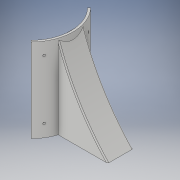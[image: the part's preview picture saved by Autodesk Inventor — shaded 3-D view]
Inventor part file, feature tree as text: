
AUTODESK INVENTOR PART (.ipt)
format: ipt  version: 2017 (Build 210142000, 142)  size: 180,736 bytes
history: native  units: in
note: dims shown in document units (in); Inventor stores cm internally (conversion verified against a paired STEP export)
features: sketch x5, extrude x3, plane x3, hole x2, shell x1, fillet x1
ambient origin geometry x8: Origin, YZ Plane, XZ Plane, XY Plane, X Axis, Y Axis, Z Axis, Center Point
bodies: Solid1 (feature_tree)
feature tree (15):
  extrude  "Extrusion1"  Depth=10.0in
  shell  "Shell2"  Thickness=3.0in
  extrude  "Extrusion6"  Depth=0.1in TaperAngle=0.0deg
  plane  "Work Plane4"
  extrude  "Extrusion7"  Depth=9.5in
  plane  "Work Plane5"
  hole  "Hole3"  [1 undecoded]
  fillet  "Fillet2"  Radius=0.25in
  plane  "Work Plane7"
  hole  "Hole5"  [1 undecoded]
  sketch  "Sketch1"  dims[d0=6.0in d1=10.0in d2=3.0in d3=0.0in]
  sketch  "Sketch10"  dims[d6=0.1in d53=0.1in d54=0.0in]
  sketch  "Sketch11"  dims[d55=10.0in d56=9.5in]
  sketch  "Sketch12"  dims[d57=9.9in d58=0.0in d59=0.25in d60=0.25in]
  sketch  "Sketch14"  dims[d61=0.25in d62=0.75in d63=0.375in d64=0.25in d65=0.5635in d66=1.0in d67=0.8108in d77=0.125in d78=0.25in d79=0.25in d80=0.25in d81=0.75in d82=0.375in d83=0.25in d84=0.5635in d85=1.0in d86=0.8108in]
note: 2 required parameter values undecoded (feature->parameter linkage not recoverable at this tier; creation-order binding heuristic only, values carry confidence <= 0.55)
